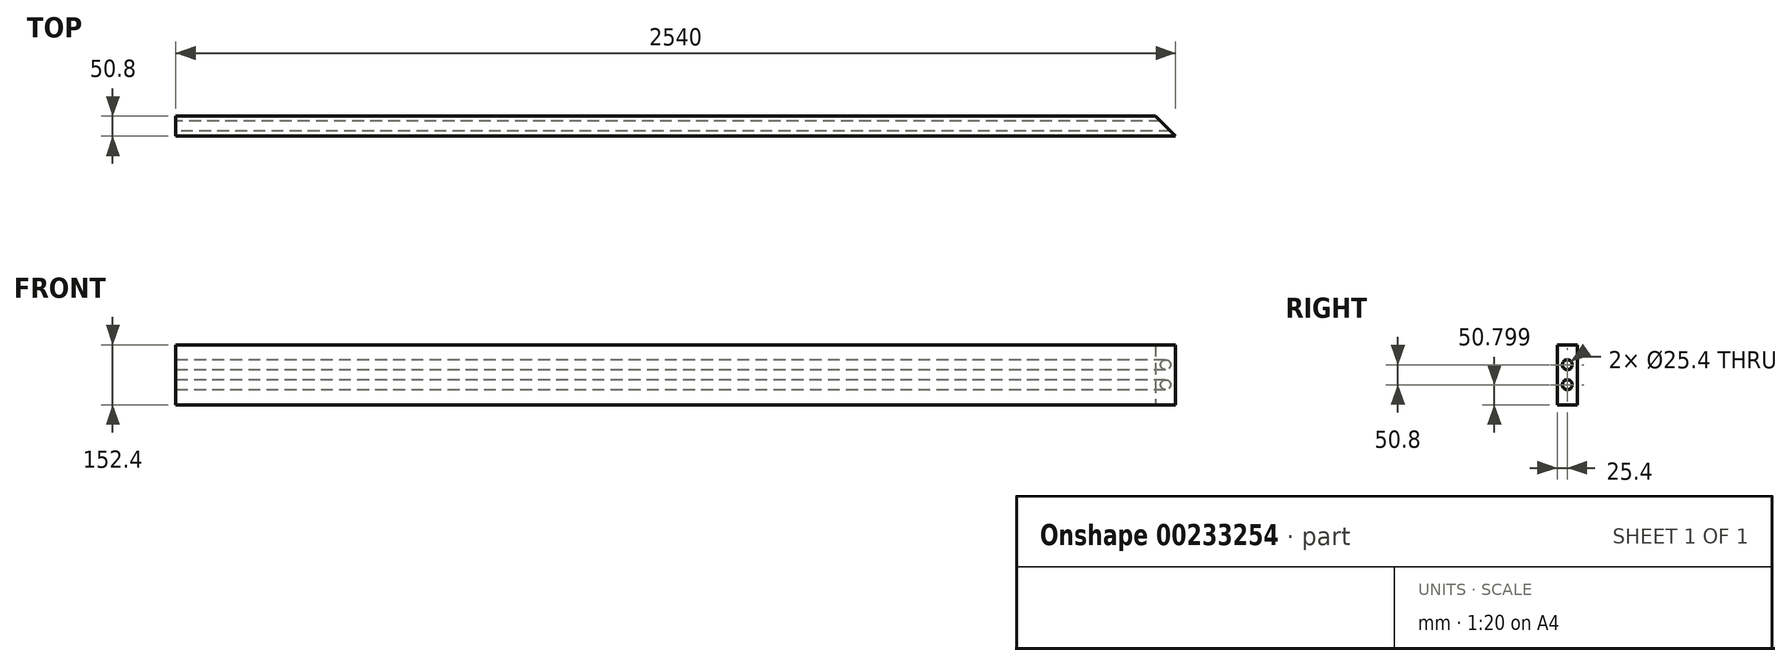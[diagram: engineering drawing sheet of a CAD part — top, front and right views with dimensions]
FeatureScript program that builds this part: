
annotation { "Feature Type Name" : "Feature", "Feature Type Description" : "" }
export const myFeature = defineFeature(function(context is Context, id is Id, definition is map)
    precondition{}
    {
        {
            var Q0;
            Q0=qCreatedBy(makeId("Front.planeOp"),FACE);
            var sketch = newSketch(context, id + "F0", { "sketchPlane" : qUnion([Q0])});
            skLineSegment(sketch, "E0.bottom", {"start": v(-273.18, 85.37) * mm, "end": v(2266.82, 85.37) * mm});
            skLineSegment(sketch, "E0.top", {"start": v(-273.18, -67.03) * mm, "end": v(2266.82, -67.03) * mm});
            skLineSegment(sketch, "E0.left", {"start": v(-273.18, 85.37) * mm, "end": v(-273.18, -67.03) * mm});
            skLineSegment(sketch, "E0.right", {"start": v(2266.82, 85.37) * mm, "end": v(2266.82, -67.03) * mm});
            skSolve(sketch);
        }
        {
            var Q0;
            Q0 = qSketchRegion(id + "F0", true);
            extrude(context, id + "F1", {"entities" : qUnion([Q0]), "depth" : 50.8 * mm});
        }
        {
            var Q0;
            Q0=makeQuery(id+"F1.opExtrude","SWEPT_FACE",FACE,{"disambiguationData":[OSD([sQuery(id+"F0.wireOp",EDGE,"E0.left")])]});
            var sketch = newSketch(context, id + "F2", { "sketchPlane" : qUnion([Q0])});
            skCircle(sketch, "E1", {"center": v(25.4, 34.57) * mm, "radius": 12.7 * mm});
            skCircle(sketch, "E2", {"center": v(25.4, -16.23) * mm, "radius": 12.7 * mm});
            skSolve(sketch);
        }
        {
            var Q0;
            Q0 = qSketchRegion(id + "F2", true);
            extrude(context, id + "F3", {"entities" : qUnion([Q0]), "operationType" : NewBodyOperationType.REMOVE, "oppositeDirection" : true, "depth" : 2540 * mm});
        }
        {
            var Q0;
            Q0=makeQuery(id+"F1.opExtrude","CAP_EDGE",EDGE,{"disambiguationData":[OSD([sQuery(id+"F0.wireOp",EDGE,"E0.right")])],"isStart":true});
            chamfer(context, id + "F4", {"entities" : qUnion([Q0]), "width" : 50.8 * mm, "tangentPropagation" : true});
        }
    });
